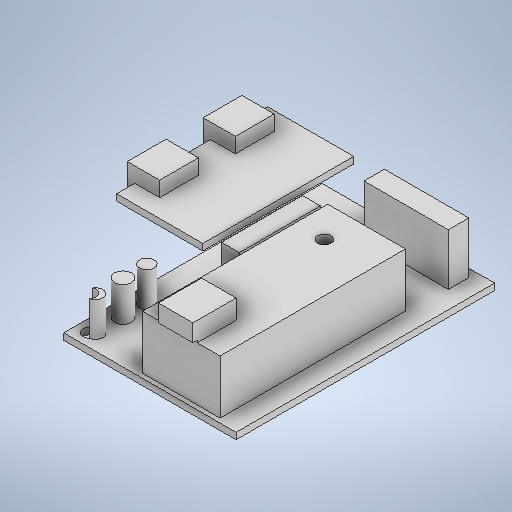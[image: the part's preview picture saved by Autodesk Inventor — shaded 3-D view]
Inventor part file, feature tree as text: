
AUTODESK INVENTOR PART (.ipt)
format: ipt  version: 2025.1 (Build 291241000, 241)  size: 358,912 bytes
history: native  units: mm
features: sketch x10, extrude x9, plane x2, hole x1
ambient origin geometry x8: Origin, YZ Plane, XZ Plane, XY Plane, X Axis, Y Axis, Z Axis, Center Point
bodies: Volumenkörper1 (feature_tree)
feature tree (22):
  extrude  "Extrusion1"  Depth=60.0mm
  extrude  "Extrusion2"  Depth=8.0mm
  extrude  "Extrusion3"  Depth=10.0mm
  plane  "Arbeitsebene1"
  extrude  "Extrusion4"  Depth=4.0mm
  extrude  "Extrusion5"  Depth=35.0mm
  extrude  "Extrusion6"  Depth=3.7mm
  extrude  "Extrusion7"  Depth=11.3mm
  extrude  "Extrusion8"  Depth=7.5mm
  extrude  "Extrusion9"  Depth=1.75mm
  plane  "Arbeitsebene2"
  hole  "Bohrung1"  [1 undecoded]
  sketch  "Skizze1"  dims[d0=40.0mm d1=60.0mm]
  sketch  "Skizze2"  dims[d2=1.5mm d3=0.0mm d4=8.0mm]
  sketch  "Skizze3"  dims[d5=10.0mm d6=10.0mm]
  sketch  "Skizze4"  dims[d7=17.0mm d8=0.0mm d9=4.0mm]
  sketch  "Skizze5"  dims[d10=1.0mm d11=0.0mm d12=35.0mm]
  sketch  "Skizze6"  dims[d13=20.0mm d14=3.7mm]
  sketch  "Skizze7"  dims[d15=29.0mm d16=11.3mm]
  sketch  "Skizze8"  dims[d17=1.5mm d18=0.0mm d19=7.5mm]
  sketch  "Skizze9"  dims[d20=9.0mm d21=1.75mm]
  sketch  "Skizze10"  dims[d22=4.2mm d23=4.2mm d24=9.0mm d25=3.5mm d26=1.5mm d27=0.0mm d28=0.0mm d29=18.0mm d30=43.0mm d31=4.7mm d32=12.5mm d33=0.0mm d34=8.0mm d35=0.0mm d36=12.0mm d37=0.0mm d38=12.0mm d39=0.0mm d40=3.0mm d41=3.0mm d42=16.0mm d43=36.5mm d44=3.1mm d45=6.0mm d46=4.0mm d47=2.0mm d48=90.0deg d49=11.8mm d50=0.0mm]
note: 1 required parameter value undecoded (feature->parameter linkage not recoverable at this tier; creation-order binding heuristic only, values carry confidence <= 0.55)
